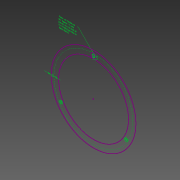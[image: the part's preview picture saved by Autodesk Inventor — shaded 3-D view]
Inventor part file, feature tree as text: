
AUTODESK INVENTOR PART (.ipt)
format: ipt  version: 2020.2 (Build 242310000, 310)  size: 83,456 bytes
history: native  units: mm
features: other x5, hole x1
ambient origin geometry x8: Origin, YZ Plane, XZ Plane, XY Plane, X Axis, Y Axis, Z Axis, Center Point
feature tree (6):
  other  "Annotations"
  other  "Plate Inner Diameter"
  hole  "Hole Locator"  [1 undecoded]
  other  "Bottom Plate for Insert Rings"
  other  "Mounting Spacer"
  other  "Leader Text 1"
note: 1 required parameter value undecoded (feature->parameter linkage not recoverable at this tier; creation-order binding heuristic only, values carry confidence <= 0.55)
